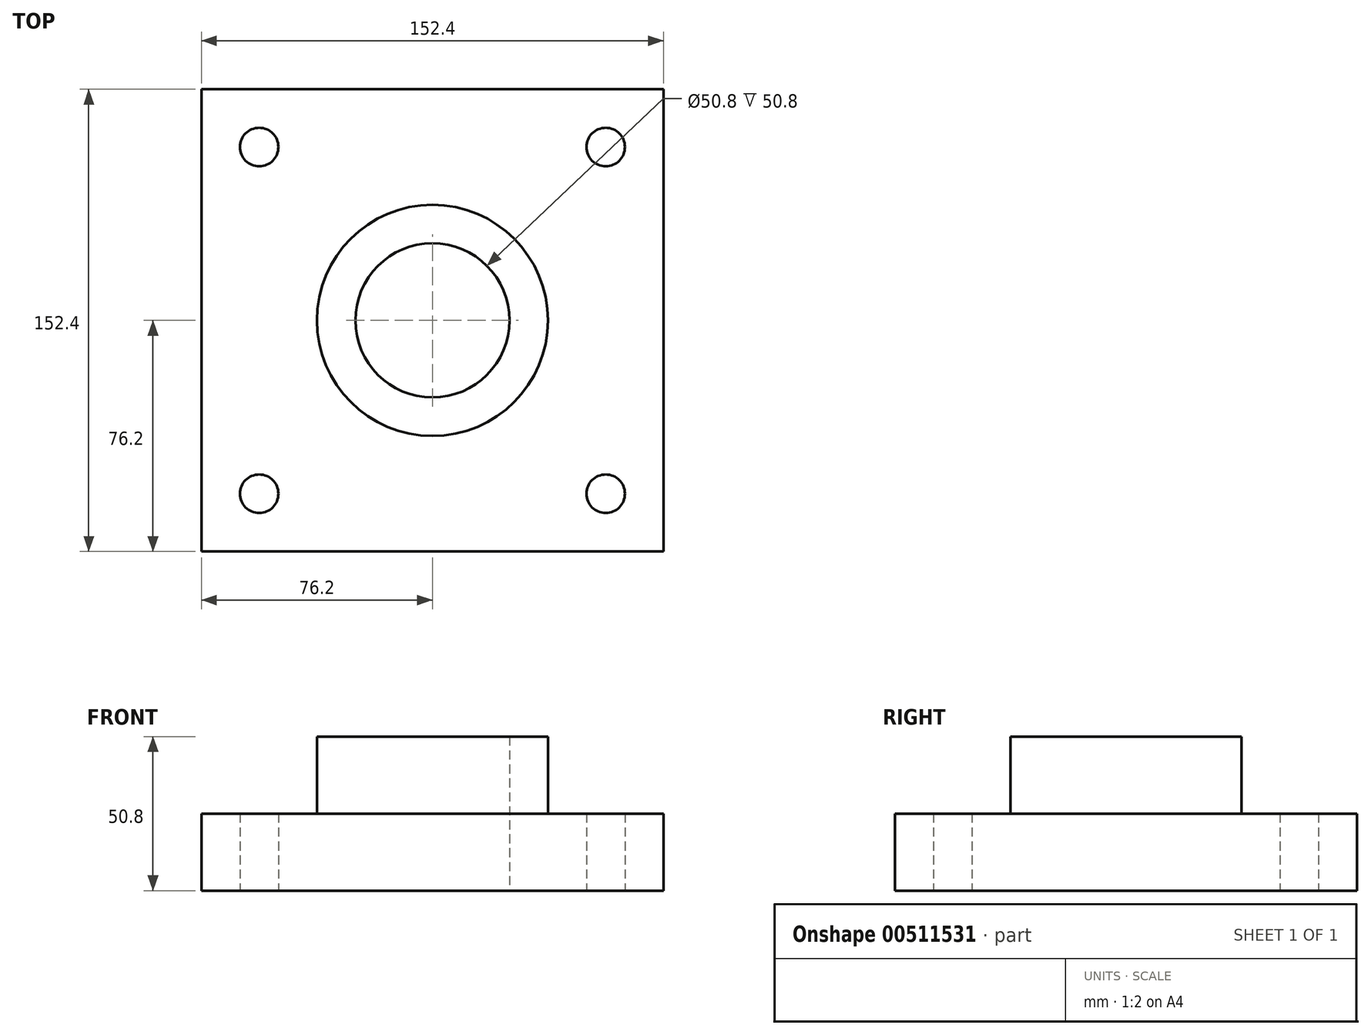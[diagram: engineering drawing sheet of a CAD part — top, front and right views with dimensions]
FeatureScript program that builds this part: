
annotation { "Feature Type Name" : "Feature", "Feature Type Description" : "" }
export const myFeature = defineFeature(function(context is Context, id is Id, definition is map)
    precondition{}
    {
        {
            var Q0;
            Q0=qCreatedBy(makeId("Top.planeOp"),FACE);
            var sketch = newSketch(context, id + "F0", { "sketchPlane" : qUnion([Q0])});
            skLineSegment(sketch, "E0.bottom", {"start": v(76.2, 76.2) * mm, "end": v(-76.2, 76.2) * mm});
            skLineSegment(sketch, "E0.top", {"start": v(76.2, -76.2) * mm, "end": v(-76.2, -76.2) * mm});
            skLineSegment(sketch, "E0.left", {"start": v(76.2, 76.2) * mm, "end": v(76.2, -76.2) * mm});
            skLineSegment(sketch, "E0.right", {"start": v(-76.2, 76.2) * mm, "end": v(-76.2, -76.2) * mm});
            skPoint(sketch, "E0.middle", {"position": v(0, 0) * mm});
            skCircle(sketch, "E1", {"center": v(0, 0) * mm, "radius": 25.4 * mm});
            skCircle(sketch, "E2", {"center": v(0, 0) * mm, "radius": 38.1 * mm});
            skCircle(sketch, "E3", {"center": v(-57.15, 57.15) * mm, "radius": 6.35 * mm});
            skCircle(sketch, "E4.0.1.0", {"center": v(-57.15, -57.15) * mm, "radius": 6.35 * mm});
            skCircle(sketch, "E4.1.0.0", {"center": v(57.15, 57.15) * mm, "radius": 6.35 * mm});
            skCircle(sketch, "E4.1.1.0", {"center": v(57.15, -57.15) * mm, "radius": 6.35 * mm});
            skLineSegment(sketch, "E4.direction1", {"start": v(-57.15, 57.15) * mm, "end": v(57.15, 57.15) * mm, "construction": true});
            skLineSegment(sketch, "E4.direction2", {"start": v(-57.15, 57.15) * mm, "end": v(-57.15, -57.15) * mm, "construction": true});
            skSolve(sketch);
        }
        {
            var Q0;
            Q0=makeQuery(id+"F0.imprint","IMPRINT",FACE,{"disambiguationData":[TD([[makeQuery(id+"F0.imprint","IMPRINT",EDGE,{"derivedFrom":sQuery(id+"F0.wireOp",EDGE,"E0.bottom")}),1.0]])]});
            extrude(context, id + "F1", {"entities" : qUnion([Q0]), "depth" : 25.4 * mm, "offsetDistance" : 25.4 * mm});
        }
        {
            var Q0;
            Q0=makeQuery(id+"F0.imprint","IMPRINT",FACE,{"disambiguationData":[TD([[makeQuery(id+"F0.imprint","IMPRINT",EDGE,{"derivedFrom":sQuery(id+"F0.wireOp",EDGE,"E1")}),-1.0]])]});
            extrude(context, id + "F2", {"entities" : qUnion([Q0]), "operationType" : NewBodyOperationType.ADD, "depth" : 50.8 * mm, "offsetDistance" : 25.4 * mm});
        }
    });
